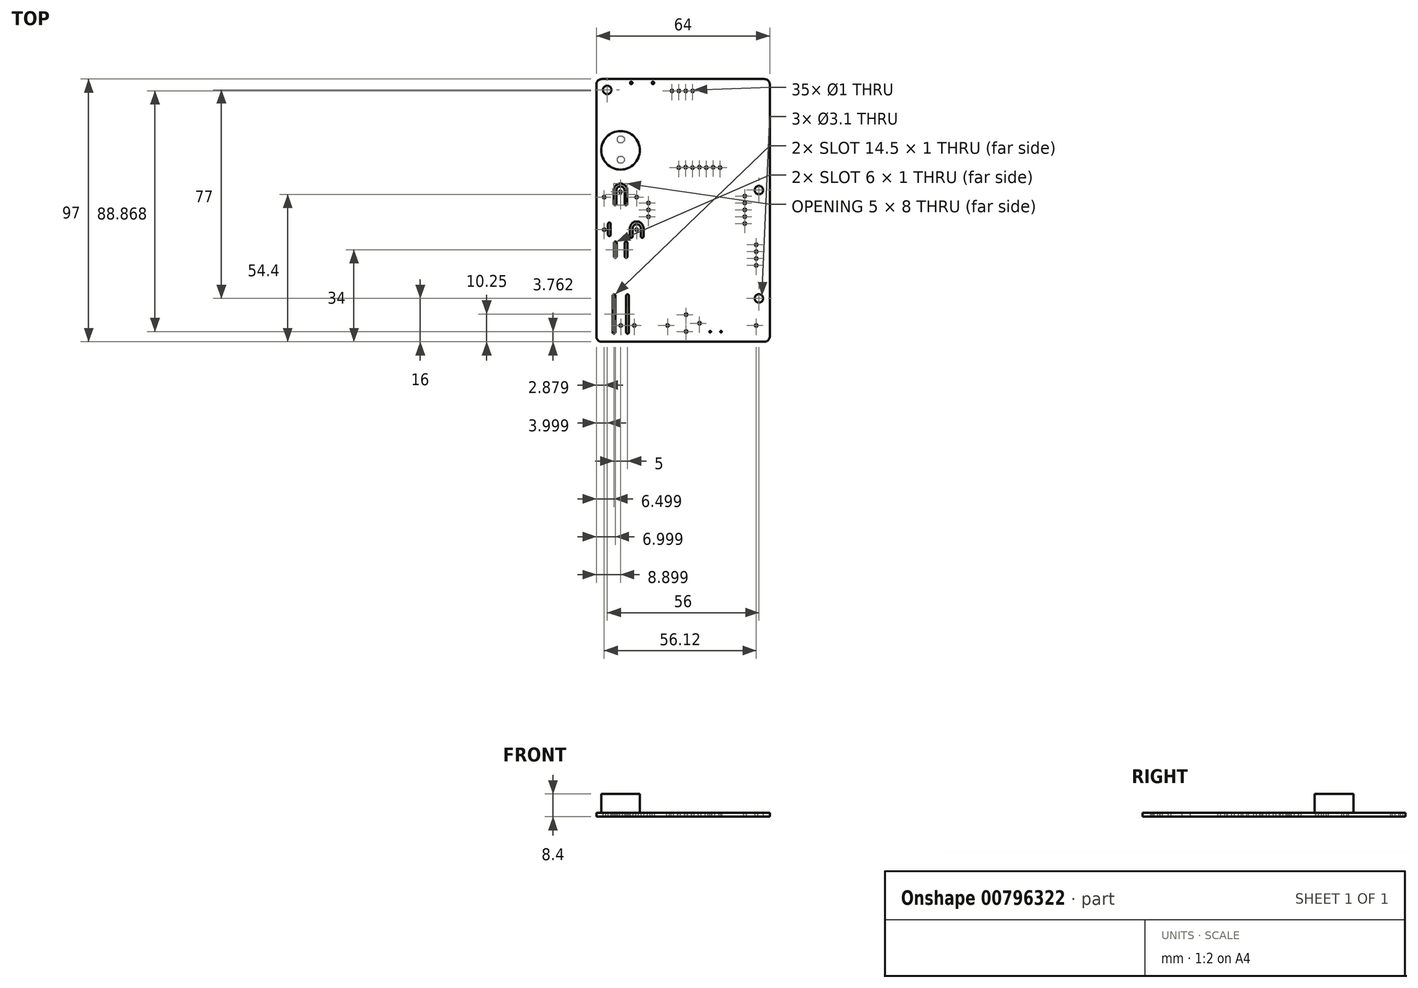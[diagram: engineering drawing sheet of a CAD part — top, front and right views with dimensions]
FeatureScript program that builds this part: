
annotation { "Feature Type Name" : "Feature", "Feature Type Description" : "" }
export const myFeature = defineFeature(function(context is Context, id is Id, definition is map)
    precondition{}
    {
        {
            var Q0;
            Q0=qCreatedBy(makeId("Top.planeOp"),FACE);
            var sketch = newSketch(context, id + "F0", { "sketchPlane" : qUnion([Q0])});
            skLineSegment(sketch, "E0", {"start": v(31.53, 48) * mm, "end": v(31.53, -45) * mm});
            skArc(sketch, "E1", {"start": v(29.53, -47) * mm, "mid": v(30.94, -46.41) * mm, "end": v(31.53, -45) * mm});
            skLineSegment(sketch, "E2", {"start": v(29.53, -47) * mm, "end": v(-30.47, -47) * mm});
            skArc(sketch, "E3", {"start": v(-32.47, -45) * mm, "mid": v(-31.89, -46.41) * mm, "end": v(-30.47, -47) * mm});
            skLineSegment(sketch, "E4", {"start": v(-32.47, -45) * mm, "end": v(-32.47, 48) * mm});
            skArc(sketch, "E5", {"start": v(-30.47, 50) * mm, "mid": v(-31.89, 49.41) * mm, "end": v(-32.47, 48) * mm});
            skLineSegment(sketch, "E6", {"start": v(-30.47, 50) * mm, "end": v(29.53, 50) * mm});
            skArc(sketch, "E7", {"start": v(31.53, 48) * mm, "mid": v(30.94, 49.41) * mm, "end": v(29.53, 50) * mm});
            skArc(sketch, "E8", {"start": v(-25.47, -30) * mm, "mid": v(-25.62, -29.65) * mm, "end": v(-25.97, -29.5) * mm});
            skLineSegment(sketch, "E9", {"start": v(-25.47, -30) * mm, "end": v(-25.47, -43.5) * mm});
            skArc(sketch, "E10", {"start": v(-25.97, -44) * mm, "mid": v(-25.62, -43.85) * mm, "end": v(-25.47, -43.5) * mm});
            skArc(sketch, "E11", {"start": v(-26.47, -43.5) * mm, "mid": v(-26.32, -43.85) * mm, "end": v(-25.97, -44) * mm});
            skLineSegment(sketch, "E12", {"start": v(-26.47, -43.5) * mm, "end": v(-26.47, -30) * mm});
            skArc(sketch, "E13", {"start": v(-25.97, -29.5) * mm, "mid": v(-26.32, -29.65) * mm, "end": v(-26.47, -30) * mm});
            skArc(sketch, "E14", {"start": v(-20.47, -30) * mm, "mid": v(-20.62, -29.65) * mm, "end": v(-20.97, -29.5) * mm});
            skLineSegment(sketch, "E15", {"start": v(-20.47, -30) * mm, "end": v(-20.47, -43.5) * mm});
            skArc(sketch, "E16", {"start": v(-20.97, -44) * mm, "mid": v(-20.62, -43.85) * mm, "end": v(-20.47, -43.5) * mm});
            skArc(sketch, "E17", {"start": v(-21.47, -43.5) * mm, "mid": v(-21.32, -43.85) * mm, "end": v(-20.97, -44) * mm});
            skLineSegment(sketch, "E18", {"start": v(-21.47, -43.5) * mm, "end": v(-21.47, -30) * mm});
            skArc(sketch, "E19", {"start": v(-20.97, -29.5) * mm, "mid": v(-21.32, -29.65) * mm, "end": v(-21.47, -30) * mm});
            skArc(sketch, "E20", {"start": v(-24.97, -10.5) * mm, "mid": v(-25.12, -10.15) * mm, "end": v(-25.47, -10) * mm});
            skLineSegment(sketch, "E21", {"start": v(-24.97, -10.5) * mm, "end": v(-24.97, -15.5) * mm});
            skArc(sketch, "E22", {"start": v(-25.47, -16) * mm, "mid": v(-25.12, -15.85) * mm, "end": v(-24.97, -15.5) * mm});
            skArc(sketch, "E23", {"start": v(-25.97, -15.5) * mm, "mid": v(-25.82, -15.85) * mm, "end": v(-25.47, -16) * mm});
            skLineSegment(sketch, "E24", {"start": v(-25.97, -15.5) * mm, "end": v(-25.97, -10.5) * mm});
            skArc(sketch, "E25", {"start": v(-25.47, -10) * mm, "mid": v(-25.82, -10.15) * mm, "end": v(-25.97, -10.5) * mm});
            skArc(sketch, "E26", {"start": v(-20.97, -10.5) * mm, "mid": v(-21.12, -10.15) * mm, "end": v(-21.47, -10) * mm});
            skLineSegment(sketch, "E27", {"start": v(-20.97, -10.5) * mm, "end": v(-20.97, -15.5) * mm});
            skArc(sketch, "E28", {"start": v(-21.47, -16) * mm, "mid": v(-21.12, -15.85) * mm, "end": v(-20.97, -15.5) * mm});
            skArc(sketch, "E29", {"start": v(-21.97, -15.5) * mm, "mid": v(-21.82, -15.85) * mm, "end": v(-21.47, -16) * mm});
            skLineSegment(sketch, "E30", {"start": v(-21.97, -15.5) * mm, "end": v(-21.97, -10.5) * mm});
            skArc(sketch, "E31", {"start": v(-21.47, -10) * mm, "mid": v(-21.82, -10.15) * mm, "end": v(-21.97, -10.5) * mm});
            skArc(sketch, "E32", {"start": v(-25.57, 3.4) * mm, "mid": v(-25.22, 3.55) * mm, "end": v(-25.07, 3.9) * mm});
            skLineSegment(sketch, "E33", {"start": v(-25.07, 3.9) * mm, "end": v(-25.07, 8.9) * mm});
            skArc(sketch, "E34", {"start": v(-23.57, 10.4) * mm, "mid": v(-24.63, 9.96) * mm, "end": v(-25.07, 8.9) * mm});
            skArc(sketch, "E35", {"start": v(-22.07, 8.9) * mm, "mid": v(-22.51, 9.96) * mm, "end": v(-23.57, 10.4) * mm});
            skLineSegment(sketch, "E36", {"start": v(-22.07, 8.9) * mm, "end": v(-22.07, 3.9) * mm});
            skArc(sketch, "E37", {"start": v(-22.07, 3.9) * mm, "mid": v(-21.92, 3.55) * mm, "end": v(-21.57, 3.4) * mm});
            skArc(sketch, "E38", {"start": v(-21.57, 3.4) * mm, "mid": v(-21.22, 3.55) * mm, "end": v(-21.07, 3.9) * mm});
            skLineSegment(sketch, "E39", {"start": v(-21.07, 3.9) * mm, "end": v(-21.07, 8.9) * mm});
            skArc(sketch, "E40", {"start": v(-21.07, 8.9) * mm, "mid": v(-21.8, 10.67) * mm, "end": v(-23.57, 11.4) * mm});
            skArc(sketch, "E41", {"start": v(-23.57, 11.4) * mm, "mid": v(-25.34, 10.67) * mm, "end": v(-26.07, 8.9) * mm});
            skLineSegment(sketch, "E42", {"start": v(-26.07, 8.9) * mm, "end": v(-26.07, 3.9) * mm});
            skArc(sketch, "E43", {"start": v(-26.07, 3.9) * mm, "mid": v(-25.92, 3.55) * mm, "end": v(-25.57, 3.4) * mm});
            skArc(sketch, "E44", {"start": v(-27.17, -3.5) * mm, "mid": v(-27.32, -3.15) * mm, "end": v(-27.67, -3) * mm});
            skLineSegment(sketch, "E45", {"start": v(-27.17, -3.5) * mm, "end": v(-27.17, -7.5) * mm});
            skArc(sketch, "E46", {"start": v(-27.67, -8) * mm, "mid": v(-27.32, -7.85) * mm, "end": v(-27.17, -7.5) * mm});
            skArc(sketch, "E47", {"start": v(-28.17, -7.5) * mm, "mid": v(-28.02, -7.85) * mm, "end": v(-27.67, -8) * mm});
            skLineSegment(sketch, "E48", {"start": v(-28.17, -7.5) * mm, "end": v(-28.17, -3.5) * mm});
            skArc(sketch, "E49", {"start": v(-27.67, -3) * mm, "mid": v(-28.02, -3.15) * mm, "end": v(-28.17, -3.5) * mm});
            skArc(sketch, "E50", {"start": v(-19.57, -8.6) * mm, "mid": v(-19.22, -8.45) * mm, "end": v(-19.07, -8.1) * mm});
            skLineSegment(sketch, "E51", {"start": v(-19.07, -8.1) * mm, "end": v(-19.07, -5.1) * mm});
            skArc(sketch, "E52", {"start": v(-17.57, -3.6) * mm, "mid": v(-18.63, -4.04) * mm, "end": v(-19.07, -5.1) * mm});
            skArc(sketch, "E53", {"start": v(-16.07, -5.1) * mm, "mid": v(-16.51, -4.04) * mm, "end": v(-17.57, -3.6) * mm});
            skLineSegment(sketch, "E54", {"start": v(-16.07, -5.1) * mm, "end": v(-16.07, -8.1) * mm});
            skArc(sketch, "E55", {"start": v(-16.07, -8.1) * mm, "mid": v(-15.92, -8.45) * mm, "end": v(-15.57, -8.6) * mm});
            skArc(sketch, "E56", {"start": v(-15.57, -8.6) * mm, "mid": v(-15.22, -8.45) * mm, "end": v(-15.07, -8.1) * mm});
            skLineSegment(sketch, "E57", {"start": v(-15.07, -8.1) * mm, "end": v(-15.07, -5.1) * mm});
            skArc(sketch, "E58", {"start": v(-15.07, -5.1) * mm, "mid": v(-15.8, -3.33) * mm, "end": v(-17.57, -2.6) * mm});
            skArc(sketch, "E59", {"start": v(-17.57, -2.6) * mm, "mid": v(-19.34, -3.33) * mm, "end": v(-20.07, -5.1) * mm});
            skLineSegment(sketch, "E60", {"start": v(-20.07, -5.1) * mm, "end": v(-20.07, -8.1) * mm});
            skArc(sketch, "E61", {"start": v(-20.07, -8.1) * mm, "mid": v(-19.92, -8.45) * mm, "end": v(-19.57, -8.6) * mm});
            skCircle(sketch, "E62", {"center": v(-28.47, 46) * mm, "radius": 1.55 * mm});
            skCircle(sketch, "E63", {"center": v(27.53, -31) * mm, "radius": 1.55 * mm});
            skCircle(sketch, "E64", {"center": v(27.53, 9) * mm, "radius": 1.55 * mm});
            skLineSegment(sketch, "E65", {"start": v(-22.48, -36.42) * mm, "end": v(-22.48, -34.44) * mm});
            skArc(sketch, "E66", {"start": v(-22.97, -34.44) * mm, "mid": v(-23.47, -33.94) * mm, "end": v(-23.97, -34.44) * mm});
            skLineSegment(sketch, "E67", {"start": v(-24.46, -34.44) * mm, "end": v(-24.46, -36.42) * mm});
            skArc(sketch, "E68", {"start": v(-23.97, -36.42) * mm, "mid": v(-23.47, -36.92) * mm, "end": v(-22.97, -36.42) * mm});
            skLineSegment(sketch, "E69", {"start": v(-22.48, -13.56) * mm, "end": v(-22.48, -11.58) * mm});
            skArc(sketch, "E70", {"start": v(-22.97, -11.58) * mm, "mid": v(-23.47, -11.08) * mm, "end": v(-23.97, -11.58) * mm});
            skLineSegment(sketch, "E71", {"start": v(-24.46, -11.58) * mm, "end": v(-24.46, -13.56) * mm});
            skArc(sketch, "E72", {"start": v(-23.97, -13.56) * mm, "mid": v(-23.47, -14.06) * mm, "end": v(-22.97, -13.56) * mm});
            skCircle(sketch, "E73", {"center": v(0.64, -37.01) * mm, "radius": 0.5 * mm});
            skCircle(sketch, "E74", {"center": v(0.64, -43.24) * mm, "radius": 0.5 * mm});
            skCircle(sketch, "E75", {"center": v(5.6, -40.19) * mm, "radius": 0.5 * mm});
            skCircle(sketch, "E76", {"center": v(26.53, -18.8) * mm, "radius": 0.5 * mm});
            skCircle(sketch, "E77", {"center": v(26.53, -16.27) * mm, "radius": 0.5 * mm});
            skCircle(sketch, "E78", {"center": v(26.53, -13.73) * mm, "radius": 0.5 * mm});
            skCircle(sketch, "E79", {"center": v(26.53, -11.19) * mm, "radius": 0.5 * mm});
            skCircle(sketch, "E80", {"center": v(-23.47, -41) * mm, "radius": 0.5 * mm});
            skCircle(sketch, "E81", {"center": v(-18.47, -41) * mm, "radius": 0.5 * mm});
            skCircle(sketch, "E82", {"center": v(26.53, -41) * mm, "radius": 0.5 * mm});
            skCircle(sketch, "E83", {"center": v(-6.17, -41) * mm, "radius": 0.5 * mm});
            skCircle(sketch, "E84", {"center": v(0.52, 45.63) * mm, "radius": 0.5 * mm});
            skCircle(sketch, "E85", {"center": v(3.06, 45.63) * mm, "radius": 0.5 * mm});
            skCircle(sketch, "E86", {"center": v(-2.02, 45.63) * mm, "radius": 0.5 * mm});
            skCircle(sketch, "E87", {"center": v(-4.56, 45.63) * mm, "radius": 0.5 * mm});
            skCircle(sketch, "E88", {"center": v(-29.6, 6.4) * mm, "radius": 0.5 * mm});
            skCircle(sketch, "E89", {"center": v(-17.6, 6.4) * mm, "radius": 0.5 * mm});
            skCircle(sketch, "E90", {"center": v(-23.6, 8.4) * mm, "radius": 0.5 * mm});
            skCircle(sketch, "E91", {"center": v(-17.6, -5.6) * mm, "radius": 0.5 * mm});
            skCircle(sketch, "E92", {"center": v(-29.6, -5.6) * mm, "radius": 0.5 * mm});
            skCircle(sketch, "E93", {"center": v(-2.05, 17.3) * mm, "radius": 0.5 * mm});
            skCircle(sketch, "E94", {"center": v(0.49, 17.44) * mm, "radius": 0.5 * mm});
            skCircle(sketch, "E95", {"center": v(3.03, 17.3) * mm, "radius": 0.5 * mm});
            skCircle(sketch, "E96", {"center": v(5.57, 17.44) * mm, "radius": 0.5 * mm});
            skCircle(sketch, "E97", {"center": v(8.1, 17.3) * mm, "radius": 0.5 * mm});
            skCircle(sketch, "E98", {"center": v(10.65, 17.44) * mm, "radius": 0.5 * mm});
            skCircle(sketch, "E99", {"center": v(13.19, 17.3) * mm, "radius": 0.5 * mm});
            skCircle(sketch, "E100", {"center": v(-11.58, 48.6) * mm, "radius": 0.44 * mm});
            skCircle(sketch, "E101", {"center": v(-19.58, 48.6) * mm, "radius": 0.44 * mm});
            skLineSegment(sketch, "E102", {"start": v(-22.94, 18.97) * mm, "end": v(-24, 18.97) * mm});
            skLineSegment(sketch, "E103", {"start": v(-24, 18.97) * mm, "end": v(-24.74, 19.71) * mm});
            skLineSegment(sketch, "E104", {"start": v(-24.74, 19.71) * mm, "end": v(-24.74, 20.77) * mm});
            skLineSegment(sketch, "E105", {"start": v(-24.74, 20.77) * mm, "end": v(-24, 21.51) * mm});
            skLineSegment(sketch, "E106", {"start": v(-24, 21.51) * mm, "end": v(-22.94, 21.51) * mm});
            skLineSegment(sketch, "E107", {"start": v(-22.94, 21.51) * mm, "end": v(-22.2, 20.77) * mm});
            skLineSegment(sketch, "E108", {"start": v(-22.2, 20.77) * mm, "end": v(-22.2, 19.71) * mm});
            skLineSegment(sketch, "E109", {"start": v(-22.2, 19.71) * mm, "end": v(-22.94, 18.97) * mm});
            skLineSegment(sketch, "E110", {"start": v(-22.94, 26.49) * mm, "end": v(-24, 26.49) * mm});
            skLineSegment(sketch, "E111", {"start": v(-24, 26.49) * mm, "end": v(-24.74, 27.23) * mm});
            skLineSegment(sketch, "E112", {"start": v(-24.74, 27.23) * mm, "end": v(-24.74, 28.29) * mm});
            skLineSegment(sketch, "E113", {"start": v(-24.74, 28.29) * mm, "end": v(-24, 29.03) * mm});
            skLineSegment(sketch, "E114", {"start": v(-24, 29.03) * mm, "end": v(-22.94, 29.03) * mm});
            skLineSegment(sketch, "E115", {"start": v(-22.94, 29.03) * mm, "end": v(-22.2, 28.29) * mm});
            skLineSegment(sketch, "E116", {"start": v(-22.2, 28.29) * mm, "end": v(-22.2, 27.23) * mm});
            skLineSegment(sketch, "E117", {"start": v(-22.2, 27.23) * mm, "end": v(-22.94, 26.49) * mm});
            skCircle(sketch, "E118", {"center": v(22.3, 6.81) * mm, "radius": 0.5 * mm});
            skCircle(sketch, "E119", {"center": v(22.3, 4.27) * mm, "radius": 0.5 * mm});
            skCircle(sketch, "E120", {"center": v(22.3, 1.73) * mm, "radius": 0.5 * mm});
            skCircle(sketch, "E121", {"center": v(22.3, -0.8) * mm, "radius": 0.5 * mm});
            skCircle(sketch, "E122", {"center": v(22.3, -3.35) * mm, "radius": 0.5 * mm});
            skCircle(sketch, "E123", {"center": v(-13.25, 4.27) * mm, "radius": 0.5 * mm});
            skCircle(sketch, "E124", {"center": v(-13.25, 1.73) * mm, "radius": 0.5 * mm});
            skCircle(sketch, "E125", {"center": v(-13.25, -0.8) * mm, "radius": 0.5 * mm});
            skCircle(sketch, "E126", {"center": v(9.53, -43.3) * mm, "radius": 0.3 * mm});
            skCircle(sketch, "E127", {"center": v(13.53, -43.3) * mm, "radius": 0.3 * mm});
            skSolve(sketch);
        }
        {
            var Q0;
            Q0 = qSketchRegion(id + "F0", true);
            extrude(context, id + "F1", {"entities" : qUnion([Q0]), "depth" : 1.4 * mm, "offsetDistance" : 25 * mm});
        }
        {
            var Q0;
            Q0=makeQuery(id+"F1.opExtrude","CAP_FACE",FACE,{"disambiguationData":[OSD([sQuery(id+"F0.wireOp",EDGE,"E0"),sQuery(id+"F0.wireOp",EDGE,"E1"),sQuery(id+"F0.wireOp",EDGE,"E2"),sQuery(id+"F0.wireOp",EDGE,"E3"),sQuery(id+"F0.wireOp",EDGE,"E4"),sQuery(id+"F0.wireOp",EDGE,"E5"),sQuery(id+"F0.wireOp",EDGE,"E6"),sQuery(id+"F0.wireOp",EDGE,"E7"),sQuery(id+"F0.wireOp",EDGE,"E8"),sQuery(id+"F0.wireOp",EDGE,"E9"),sQuery(id+"F0.wireOp",EDGE,"E10"),sQuery(id+"F0.wireOp",EDGE,"E11"),sQuery(id+"F0.wireOp",EDGE,"E12"),sQuery(id+"F0.wireOp",EDGE,"E13"),sQuery(id+"F0.wireOp",EDGE,"E14"),sQuery(id+"F0.wireOp",EDGE,"E15"),sQuery(id+"F0.wireOp",EDGE,"E16"),sQuery(id+"F0.wireOp",EDGE,"E17"),sQuery(id+"F0.wireOp",EDGE,"E18"),sQuery(id+"F0.wireOp",EDGE,"E19"),sQuery(id+"F0.wireOp",EDGE,"E20"),sQuery(id+"F0.wireOp",EDGE,"E21"),sQuery(id+"F0.wireOp",EDGE,"E22"),sQuery(id+"F0.wireOp",EDGE,"E23"),sQuery(id+"F0.wireOp",EDGE,"E24"),sQuery(id+"F0.wireOp",EDGE,"E25"),sQuery(id+"F0.wireOp",EDGE,"E26"),sQuery(id+"F0.wireOp",EDGE,"E27"),sQuery(id+"F0.wireOp",EDGE,"E28"),sQuery(id+"F0.wireOp",EDGE,"E29"),sQuery(id+"F0.wireOp",EDGE,"E30"),sQuery(id+"F0.wireOp",EDGE,"E31"),sQuery(id+"F0.wireOp",EDGE,"E32"),sQuery(id+"F0.wireOp",EDGE,"E33"),sQuery(id+"F0.wireOp",EDGE,"E34"),sQuery(id+"F0.wireOp",EDGE,"E35"),sQuery(id+"F0.wireOp",EDGE,"E36"),sQuery(id+"F0.wireOp",EDGE,"E37"),sQuery(id+"F0.wireOp",EDGE,"E38"),sQuery(id+"F0.wireOp",EDGE,"E39"),sQuery(id+"F0.wireOp",EDGE,"E40"),sQuery(id+"F0.wireOp",EDGE,"E41"),sQuery(id+"F0.wireOp",EDGE,"E42"),sQuery(id+"F0.wireOp",EDGE,"E43"),sQuery(id+"F0.wireOp",EDGE,"E44"),sQuery(id+"F0.wireOp",EDGE,"E45"),sQuery(id+"F0.wireOp",EDGE,"E46"),sQuery(id+"F0.wireOp",EDGE,"E47"),sQuery(id+"F0.wireOp",EDGE,"E48"),sQuery(id+"F0.wireOp",EDGE,"E49"),sQuery(id+"F0.wireOp",EDGE,"E50"),sQuery(id+"F0.wireOp",EDGE,"E51"),sQuery(id+"F0.wireOp",EDGE,"E52"),sQuery(id+"F0.wireOp",EDGE,"E53"),sQuery(id+"F0.wireOp",EDGE,"E54"),sQuery(id+"F0.wireOp",EDGE,"E55"),sQuery(id+"F0.wireOp",EDGE,"E56"),sQuery(id+"F0.wireOp",EDGE,"E57"),sQuery(id+"F0.wireOp",EDGE,"E58"),sQuery(id+"F0.wireOp",EDGE,"E59"),sQuery(id+"F0.wireOp",EDGE,"E60"),sQuery(id+"F0.wireOp",EDGE,"E61"),sQuery(id+"F0.wireOp",EDGE,"E62"),sQuery(id+"F0.wireOp",EDGE,"E63"),sQuery(id+"F0.wireOp",EDGE,"E64"),sQuery(id+"F0.wireOp",EDGE,"E73"),sQuery(id+"F0.wireOp",EDGE,"E74"),sQuery(id+"F0.wireOp",EDGE,"E75"),sQuery(id+"F0.wireOp",EDGE,"E76"),sQuery(id+"F0.wireOp",EDGE,"E77"),sQuery(id+"F0.wireOp",EDGE,"E78"),sQuery(id+"F0.wireOp",EDGE,"E79"),sQuery(id+"F0.wireOp",EDGE,"E80"),sQuery(id+"F0.wireOp",EDGE,"E81"),sQuery(id+"F0.wireOp",EDGE,"E82"),sQuery(id+"F0.wireOp",EDGE,"E83"),sQuery(id+"F0.wireOp",EDGE,"E84"),sQuery(id+"F0.wireOp",EDGE,"E85"),sQuery(id+"F0.wireOp",EDGE,"E86"),sQuery(id+"F0.wireOp",EDGE,"E87"),sQuery(id+"F0.wireOp",EDGE,"E88"),sQuery(id+"F0.wireOp",EDGE,"E89"),sQuery(id+"F0.wireOp",EDGE,"E90"),sQuery(id+"F0.wireOp",EDGE,"E91"),sQuery(id+"F0.wireOp",EDGE,"E92"),sQuery(id+"F0.wireOp",EDGE,"E93"),sQuery(id+"F0.wireOp",EDGE,"E94"),sQuery(id+"F0.wireOp",EDGE,"E95"),sQuery(id+"F0.wireOp",EDGE,"E96"),sQuery(id+"F0.wireOp",EDGE,"E97"),sQuery(id+"F0.wireOp",EDGE,"E98"),sQuery(id+"F0.wireOp",EDGE,"E99"),sQuery(id+"F0.wireOp",EDGE,"E100"),sQuery(id+"F0.wireOp",EDGE,"E101"),sQuery(id+"F0.wireOp",EDGE,"E102"),sQuery(id+"F0.wireOp",EDGE,"E103"),sQuery(id+"F0.wireOp",EDGE,"E104"),sQuery(id+"F0.wireOp",EDGE,"E105"),sQuery(id+"F0.wireOp",EDGE,"E106"),sQuery(id+"F0.wireOp",EDGE,"E107"),sQuery(id+"F0.wireOp",EDGE,"E108"),sQuery(id+"F0.wireOp",EDGE,"E109"),sQuery(id+"F0.wireOp",EDGE,"E110"),sQuery(id+"F0.wireOp",EDGE,"E111"),sQuery(id+"F0.wireOp",EDGE,"E112"),sQuery(id+"F0.wireOp",EDGE,"E113"),sQuery(id+"F0.wireOp",EDGE,"E114"),sQuery(id+"F0.wireOp",EDGE,"E115"),sQuery(id+"F0.wireOp",EDGE,"E116"),sQuery(id+"F0.wireOp",EDGE,"E117"),sQuery(id+"F0.wireOp",EDGE,"E118"),sQuery(id+"F0.wireOp",EDGE,"E119"),sQuery(id+"F0.wireOp",EDGE,"E120"),sQuery(id+"F0.wireOp",EDGE,"E121"),sQuery(id+"F0.wireOp",EDGE,"E122"),sQuery(id+"F0.wireOp",EDGE,"E123"),sQuery(id+"F0.wireOp",EDGE,"E124"),sQuery(id+"F0.wireOp",EDGE,"E125"),sQuery(id+"F0.wireOp",EDGE,"E126"),sQuery(id+"F0.wireOp",EDGE,"E127")])],"isStart":false});
            var sketch = newSketch(context, id + "F2", { "sketchPlane" : qUnion([Q0])});
            skCircle(sketch, "E128", {"center": v(-23.55, 23.7) * mm, "radius": 7.12 * mm});
            skSolve(sketch);
        }
        {
            var Q0;
            Q0 = qSketchRegion(id + "F2", true);
            extrude(context, id + "F3", {"entities" : qUnion([Q0]), "depth" : 7 * mm, "offsetDistance" : 25 * mm});
        }
    });
